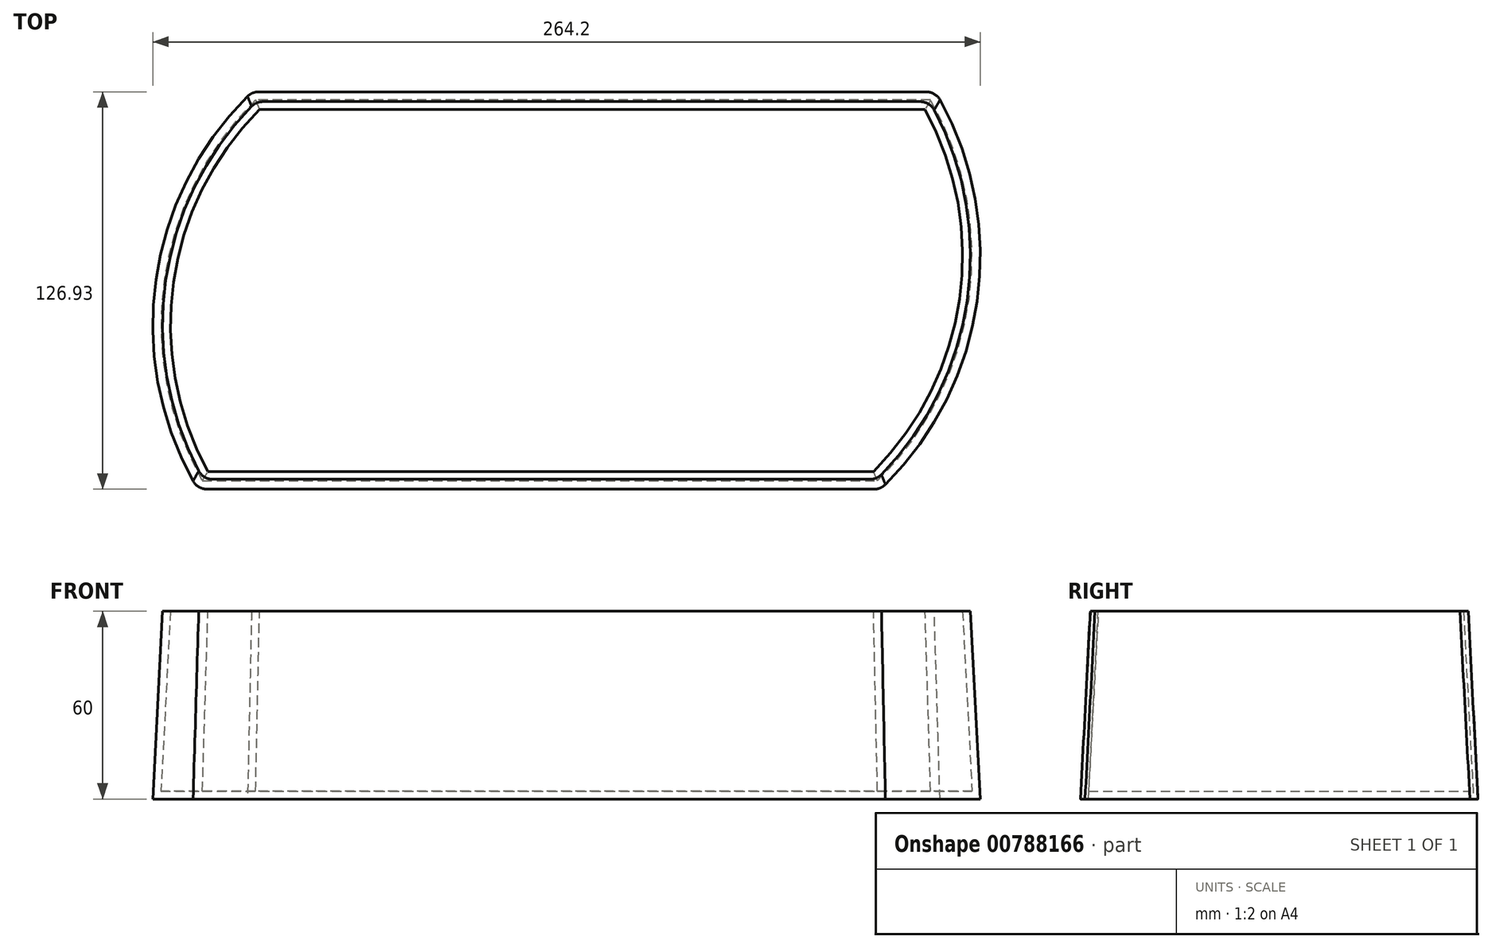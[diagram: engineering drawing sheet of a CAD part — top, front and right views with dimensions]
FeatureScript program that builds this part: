
annotation { "Feature Type Name" : "Feature", "Feature Type Description" : "" }
export const myFeature = defineFeature(function(context is Context, id is Id, definition is map)
    precondition{}
    {
        {
            var Q0;
            Q0=qCreatedBy(makeId("Top.planeOp"),FACE);
            var sketch = newSketch(context, id + "F0", { "sketchPlane" : qUnion([Q0])});
            skLineSegment(sketch, "E0.bottom", {"start": v(-97.88, 42.65) * mm, "end": v(117.12, 42.65) * mm});
            skLineSegment(sketch, "E0.top", {"start": v(-114.78, -77.99) * mm, "end": v(100.22, -77.99) * mm});
            skLineSegment(sketch, "E0.left", {"start": v(-97.88, 42.65) * mm, "end": v(-97.88, 42.65) * mm});
            skLineSegment(sketch, "E1", {"start": v(-114.78, -77.99) * mm, "end": v(-114.78, -77.99) * mm});
            skArc(sketch, "E2", {"start": v(100.22, -77.99) * mm, "mid": v(129.16, -20.54) * mm, "end": v(117.12, 42.65) * mm});
            skArc(sketch, "E3", {"start": v(-97.88, 42.65) * mm, "mid": v(-126.82, -14.8) * mm, "end": v(-114.78, -77.99) * mm});
            skSolve(sketch);
        }
        {
            var Q0;
            Q0=makeQuery(id+"F0.imprint","IMPRINT",FACE,{"disambiguationData":[TD([[makeQuery(id+"F0.imprint","IMPRINT",EDGE,{"derivedFrom":sQuery(id+"F0.wireOp",EDGE,"E0.bottom")}),-1.0]])]});
            extrude(context, id + "F1", {"entities" : qUnion([Q0]), "oppositeDirection" : true, "depth" : 60 * mm, "offsetDistance" : 25 * mm, "hasDraft" : true, "draftAngle" : 3 * degree});
        }
        {
            var Q0;
            Q0=makeQuery(id+"F1.opExtrude","CAP_FACE",FACE,{"disambiguationData":[OSD([sQuery(id+"F0.wireOp",EDGE,"E0.bottom"),sQuery(id+"F0.wireOp",EDGE,"E0.top"),sQuery(id+"F0.wireOp",EDGE,"E2"),sQuery(id+"F0.wireOp",EDGE,"E3")])],"isStart":true});
            shell(context, id + "F2", {"entities" : qUnion([Q0]), "thickness" : 2.5 * mm});
        }
        {
            var Q0;
            Q0=makeQuery(id+"F1.opExtrude","SWEPT_EDGE",EDGE,{"disambiguationData":[OSD([sQuery(id+"F0.wireOp",EDGE,"E0.top"),sQuery(id+"F0.wireOp",EDGE,"E2")])]});
            var Q1;
            Q1=makeQuery(id+"F1.opExtrude","SWEPT_EDGE",EDGE,{"disambiguationData":[OSD([sQuery(id+"F0.wireOp",EDGE,"E0.top"),sQuery(id+"F0.wireOp",EDGE,"E3")])]});
            var Q2;
            Q2=makeQuery(id+"F1.opExtrude","SWEPT_EDGE",EDGE,{"disambiguationData":[OSD([sQuery(id+"F0.wireOp",EDGE,"E0.bottom"),sQuery(id+"F0.wireOp",EDGE,"E3")])]});
            var Q3;
            Q3=makeQuery(id+"F1.opExtrude","SWEPT_EDGE",EDGE,{"disambiguationData":[OSD([sQuery(id+"F0.wireOp",EDGE,"E0.bottom"),sQuery(id+"F0.wireOp",EDGE,"E2")])]});
            fillet(context, id + "F3", {"entities" : qUnion([Q0, Q1, Q2, Q3]), "radius" : 5 * mm, "tangentPropagation" : true, "allowEdgeOverflow" : false});
        }
    });
